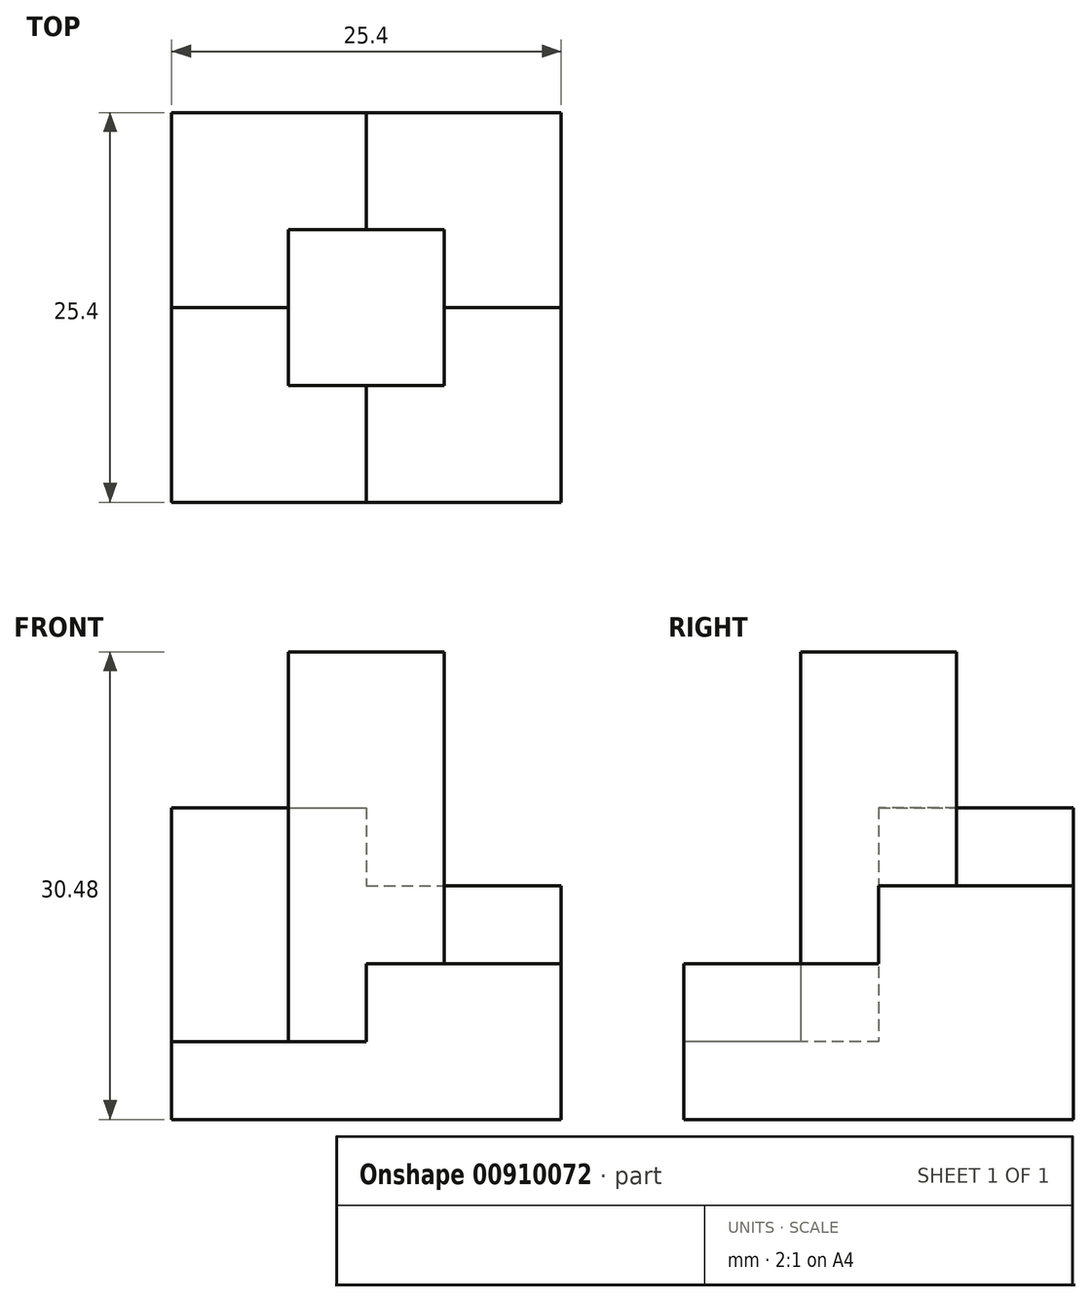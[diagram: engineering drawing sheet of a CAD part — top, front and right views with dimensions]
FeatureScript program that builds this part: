
annotation { "Feature Type Name" : "Feature", "Feature Type Description" : "" }
export const myFeature = defineFeature(function(context is Context, id is Id, definition is map)
    precondition{}
    {
        {
            var Q0;
            Q0=qCreatedBy(makeId("Top.planeOp"),FACE);
            var sketch = newSketch(context, id + "F0", { "sketchPlane" : qUnion([Q0])});
            skLineSegment(sketch, "E0.bottom", {"start": v(-9.35, 12.73) * mm, "end": v(10.97, 12.73) * mm});
            skLineSegment(sketch, "E0.top", {"start": v(-9.35, -12.67) * mm, "end": v(10.97, -12.67) * mm});
            skLineSegment(sketch, "E0.left", {"start": v(-11.9, 10.2) * mm, "end": v(-11.9, -10.13) * mm});
            skLineSegment(sketch, "E0.right", {"start": v(13.5, 10.2) * mm, "end": v(13.5, -10.13) * mm});
            skLineSegment(sketch, "E1.bottom", {"start": v(-4.27, 5.11) * mm, "end": v(5.89, 5.11) * mm});
            skLineSegment(sketch, "E1.top", {"start": v(-4.27, -5.05) * mm, "end": v(5.89, -5.05) * mm});
            skLineSegment(sketch, "E1.left", {"start": v(-4.27, 5.11) * mm, "end": v(-4.27, -5.05) * mm});
            skLineSegment(sketch, "E1.right", {"start": v(5.89, 5.11) * mm, "end": v(5.89, -5.05) * mm});
            skLineSegment(sketch, "E2.left", {"start": v(-4.27, -1.4) * mm, "end": v(-4.27, -1.4) * mm});
            skLineSegment(sketch, "E2.right", {"start": v(-11.9, 0.78) * mm, "end": v(-11.9, 0.78) * mm});
            skLineSegment(sketch, "E3", {"start": v(-4.27, 0.03) * mm, "end": v(-11.9, 0.03) * mm});
            skLineSegment(sketch, "E4", {"start": v(5.89, 0.03) * mm, "end": v(13.5, 0.03) * mm});
            skLineSegment(sketch, "E5", {"start": v(0.8, 5.11) * mm, "end": v(0.8, 12.73) * mm});
            skLineSegment(sketch, "E6", {"start": v(0.8, -5.05) * mm, "end": v(0.8, -12.67) * mm});
            skPoint(sketch, "E7.visualSharp", {"position": v(-11.9, 12.73) * mm});
            skPoint(sketch, "E8.visualSharp", {"position": v(13.5, 12.73) * mm});
            skPoint(sketch, "E9.visualSharp", {"position": v(13.5, -12.67) * mm});
            skPoint(sketch, "E10.visualSharp", {"position": v(-11.9, -12.67) * mm});
            skLineSegment(sketch, "E11", {"start": v(-11.9, 10.2) * mm, "end": v(-11.9, 12.73) * mm});
            skLineSegment(sketch, "E12", {"start": v(-9.35, 12.73) * mm, "end": v(-11.9, 12.73) * mm});
            skLineSegment(sketch, "E13", {"start": v(10.97, 12.73) * mm, "end": v(13.5, 12.73) * mm});
            skLineSegment(sketch, "E14", {"start": v(13.5, 12.73) * mm, "end": v(13.5, 10.2) * mm});
            skLineSegment(sketch, "E15", {"start": v(13.5, -10.13) * mm, "end": v(13.5, -12.67) * mm});
            skLineSegment(sketch, "E16", {"start": v(10.97, -12.67) * mm, "end": v(13.5, -12.67) * mm});
            skLineSegment(sketch, "E17", {"start": v(-9.35, -12.67) * mm, "end": v(-11.9, -12.67) * mm});
            skLineSegment(sketch, "E18", {"start": v(-11.9, -10.13) * mm, "end": v(-11.9, -12.67) * mm});
            skSolve(sketch);
        }
        {
            var Q0;
            {var subQ3=sQuery(id+"F0.wireOp",EDGE,"E3");Q0=makeQuery(id+"F0.imprint","IMPRINT",FACE,{"disambiguationData":[TD([[makeQuery(id+"F0.imprint","IMPRINT",EDGE,{"derivedFrom":subQ3}),-1.0]])]});}
            extrude(context, id + "F1", {"entities" : qUnion([Q0]), "depth" : 20.32 * mm, "offsetDistance" : 25.4 * mm});
        }
        {
            var Q0;
            {var subQ3=sQuery(id+"F0.wireOp",EDGE,"E4");Q0=makeQuery(id+"F0.imprint","IMPRINT",FACE,{"disambiguationData":[TD([[makeQuery(id+"F0.imprint","IMPRINT",EDGE,{"derivedFrom":subQ3}),1.0]])]});}
            extrude(context, id + "F2", {"entities" : qUnion([Q0]), "operationType" : NewBodyOperationType.ADD, "depth" : 15.24 * mm, "offsetDistance" : 25.4 * mm});
        }
        {
            var Q0;
            {var subQ4=sQuery(id+"F0.wireOp",EDGE,"E1.left");var subQ6=sQuery(id+"F0.wireOp",EDGE,"E1.bottom");var subQ9=makeQuery(id+"F0.imprint","INTERSECT",VERTEX,{"derivedFrom":[subQ6,subQ4]});Q0=makeQuery(id+"F0.imprint","IMPRINT",FACE,{"disambiguationData":[TD([[makeQuery(id+"F0.imprint","IMPRINT",EDGE,{"disambiguationData":[TD([[subQ9,-1.0]])],"derivedFrom":subQ6}),-1.0]])]});}
            extrude(context, id + "F3", {"entities" : qUnion([Q0]), "operationType" : NewBodyOperationType.ADD, "depth" : 25.4 * mm, "offsetDistance" : 25.4 * mm});
        }
        {
            var Q0;
            {var subQ3=sQuery(id+"F0.wireOp",EDGE,"E4");Q0=makeQuery(id+"F0.imprint","IMPRINT",FACE,{"disambiguationData":[TD([[makeQuery(id+"F0.imprint","IMPRINT",EDGE,{"derivedFrom":subQ3}),-1.0]])]});}
            extrude(context, id + "F4", {"entities" : qUnion([Q0]), "operationType" : NewBodyOperationType.ADD, "depth" : 10.16 * mm, "offsetDistance" : 25.4 * mm});
        }
        {
            var Q0;
            {var subQ3=sQuery(id+"F0.wireOp",EDGE,"E3");Q0=makeQuery(id+"F0.imprint","IMPRINT",FACE,{"disambiguationData":[TD([[makeQuery(id+"F0.imprint","IMPRINT",EDGE,{"derivedFrom":subQ3}),1.0]])]});}
            var Q1;
            Q1=makeQuery(id+"F3.opExtrude","CAP_FACE",FACE,{"disambiguationData":[OSD([sQuery(id+"F0.wireOp",EDGE,"E1.bottom"),sQuery(id+"F0.wireOp",EDGE,"E1.top"),sQuery(id+"F0.wireOp",EDGE,"E1.left"),sQuery(id+"F0.wireOp",EDGE,"E1.right")])],"isStart":false});
            extrude(context, id + "F5", {"entities" : qUnion([Q0, Q1]), "operationType" : NewBodyOperationType.ADD, "depth" : 5.08 * mm, "offsetDistance" : 25.4 * mm});
        }
    });
